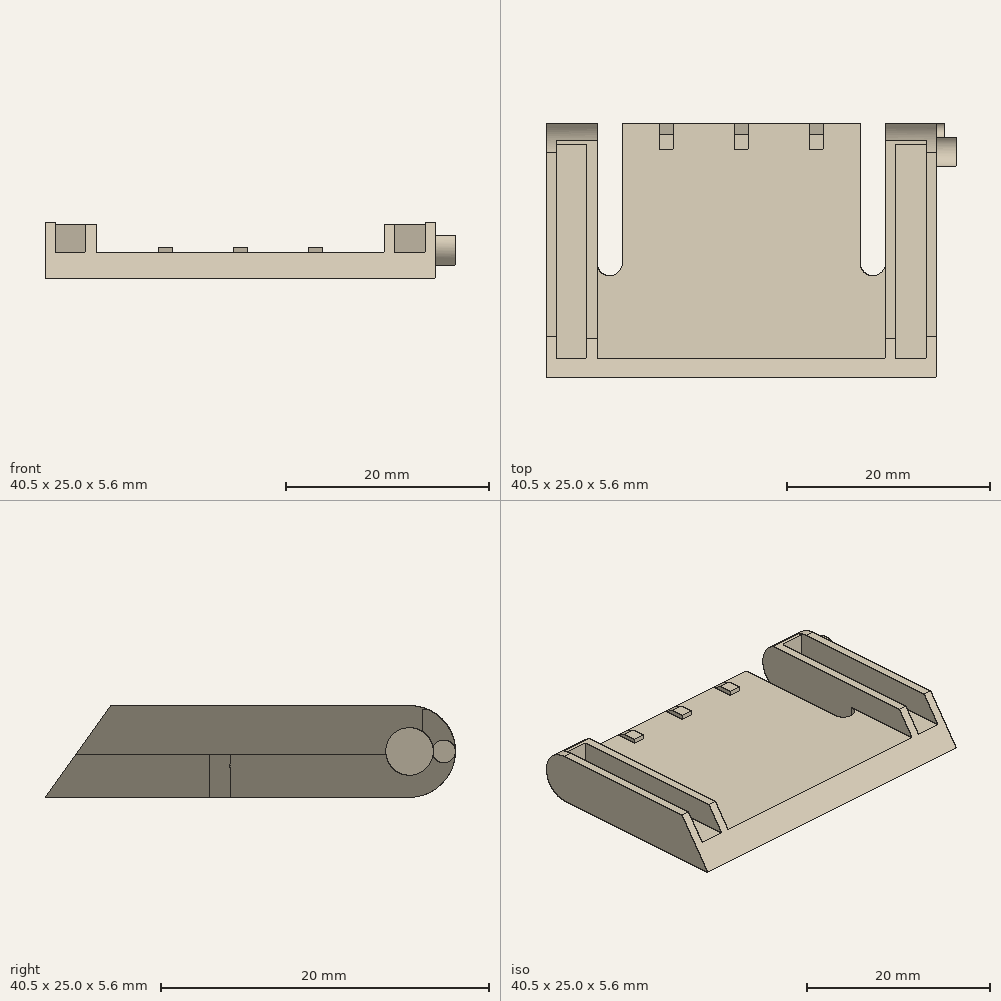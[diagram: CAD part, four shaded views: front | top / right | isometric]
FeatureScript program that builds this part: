
annotation { "Feature Type Name" : "Feature", "Feature Type Description" : "" }
export const myFeature = defineFeature(function(context is Context, id is Id, definition is map)
    precondition{}
    {
        {
            var Q0;
            Q0=qCreatedBy(makeId("Top.planeOp"),FACE);
            var sketch = newSketch(context, id + "F0", { "sketchPlane" : qUnion([Q0])});
            skLineSegment(sketch, "E0.bottom", {"start": v(19.25, -12.5) * mm, "end": v(-19.25, -12.5) * mm});
            skLineSegment(sketch, "E0.top", {"start": v(19.25, 12.5) * mm, "end": v(-19.25, 12.5) * mm});
            skLineSegment(sketch, "E0.left", {"start": v(19.25, -12.5) * mm, "end": v(19.25, 12.5) * mm});
            skLineSegment(sketch, "E0.right", {"start": v(-19.25, -12.5) * mm, "end": v(-19.25, 12.5) * mm});
            skPoint(sketch, "E0.middle", {"position": v(0, 0) * mm});
            skSolve(sketch);
        }
        {
            var Q0;
            Q0 = qSketchRegion(id + "F0", true);
            extrude(context, id + "F1", {"entities" : qUnion([Q0]), "depth" : 2.6 * mm});
        }
        {
            var Q0;
            Q0=makeQuery(id+"F1.opExtrude","CAP_FACE",FACE,{"disambiguationData":[OSD([sQuery(id+"F0.wireOp",EDGE,"E0.bottom"),sQuery(id+"F0.wireOp",EDGE,"E0.top"),sQuery(id+"F0.wireOp",EDGE,"E0.left"),sQuery(id+"F0.wireOp",EDGE,"E0.right")])],"isStart":false});
            var sketch = newSketch(context, id + "F2", { "sketchPlane" : qUnion([Q0])});
            skLineSegment(sketch, "E1.bottom", {"start": v(-14.25, 12.5) * mm, "end": v(-11.75, 12.5) * mm});
            skLineSegment(sketch, "E1.top", {"start": v(-13, -2.5) * mm, "end": v(-13, -2.5) * mm});
            skLineSegment(sketch, "E1.left", {"start": v(-14.25, 12.5) * mm, "end": v(-14.25, -1.25) * mm});
            skLineSegment(sketch, "E1.right", {"start": v(-11.75, 12.5) * mm, "end": v(-11.75, -1.25) * mm});
            skLineSegment(sketch, "E2", {"start": v(0, 12.5) * mm, "end": v(0, -12.5) * mm});
            skLineSegment(sketch, "E3.MirrorCS", {"start": v(14.25, 12.5) * mm, "end": v(11.75, 12.5) * mm});
            skLineSegment(sketch, "E4.MirrorCS", {"start": v(14.25, 12.5) * mm, "end": v(14.25, -1.25) * mm});
            skLineSegment(sketch, "E5.MirrorCS", {"start": v(11.75, 12.5) * mm, "end": v(11.75, -1.25) * mm});
            skLineSegment(sketch, "E6.MirrorCS", {"start": v(13, -2.5) * mm, "end": v(13, -2.5) * mm});
            skPoint(sketch, "E7.visualSharp", {"position": v(-14.25, -2.5) * mm});
            skArc(sketch, "E7.filletArc", {"start": v(-14.25, -1.25) * mm, "mid": v(-13.88, -2.13) * mm, "end": v(-13, -2.5) * mm});
            skPoint(sketch, "E8.visualSharp", {"position": v(-11.75, -2.5) * mm});
            skArc(sketch, "E8.filletArc", {"start": v(-13, -2.5) * mm, "mid": v(-12.12, -2.13) * mm, "end": v(-11.75, -1.25) * mm});
            skPoint(sketch, "E9.visualSharp", {"position": v(11.75, -2.5) * mm});
            skArc(sketch, "E9.filletArc", {"start": v(11.75, -1.25) * mm, "mid": v(12.12, -2.13) * mm, "end": v(13, -2.5) * mm});
            skPoint(sketch, "E10.visualSharp", {"position": v(14.25, -2.5) * mm});
            skArc(sketch, "E10.filletArc", {"start": v(13, -2.5) * mm, "mid": v(13.88, -2.13) * mm, "end": v(14.25, -1.25) * mm});
            skSolve(sketch);
        }
        {
            var Q0;
            Q0 = qSketchRegion(id + "F2", true);
            extrude(context, id + "F3", {"entities" : qUnion([Q0]), "operationType" : NewBodyOperationType.REMOVE, "endBound" : BoundingType.THROUGH_ALL, "oppositeDirection" : true, "depth" : 25 * mm});
        }
        {
            var Q0;
            Q0=makeQuery(id+"F1.opExtrude","CAP_FACE",FACE,{"disambiguationData":[OSD([sQuery(id+"F0.wireOp",EDGE,"E0.bottom"),sQuery(id+"F0.wireOp",EDGE,"E0.top"),sQuery(id+"F0.wireOp",EDGE,"E0.left"),sQuery(id+"F0.wireOp",EDGE,"E0.right")])],"isStart":false});
            var sketch = newSketch(context, id + "F4", { "sketchPlane" : qUnion([Q0])});
            skLineSegment(sketch, "E11.bottom", {"start": v(-19.25, 12.5) * mm, "end": v(-14.25, 12.5) * mm});
            skLineSegment(sketch, "E11.top", {"start": v(-19.25, -12.5) * mm, "end": v(-14.25, -12.5) * mm});
            skLineSegment(sketch, "E11.left", {"start": v(-19.25, 12.5) * mm, "end": v(-19.25, -12.5) * mm});
            skLineSegment(sketch, "E11.right", {"start": v(-14.25, 12.5) * mm, "end": v(-14.25, -12.5) * mm});
            skPoint(sketch, "E12.oppositeSnap0", {"position": v(14.25, 5.62) * mm});
            skLineSegment(sketch, "E12.bottom", {"start": v(19.25, 12.5) * mm, "end": v(14.25, 12.5) * mm});
            skLineSegment(sketch, "E12.top", {"start": v(19.25, -12.5) * mm, "end": v(14.25, -12.5) * mm});
            skLineSegment(sketch, "E12.left", {"start": v(19.25, 12.5) * mm, "end": v(19.25, -12.5) * mm});
            skLineSegment(sketch, "E12.right", {"start": v(14.25, 12.5) * mm, "end": v(14.25, -12.5) * mm});
            skSolve(sketch);
        }
        {
            var Q0;
            Q0 = qSketchRegion(id + "F4", true);
            extrude(context, id + "F5", {"entities" : qUnion([Q0]), "operationType" : NewBodyOperationType.ADD, "depth" : 3 * mm});
        }
        {
            var Q0;
            Q0=makeQuery(id+"F5.boolean.opBoolean","MERGE",FACE,{"derivedFrom":[makeQuery(id+"F1.opExtrude","SWEPT_FACE",FACE,{"disambiguationData":[OSD([sQuery(id+"F0.wireOp",EDGE,"E0.bottom")])]}),makeQuery(id+"F5.opExtrude","SWEPT_FACE",FACE,{"disambiguationData":[OSD([sQuery(id+"F4.wireOp",EDGE,"E11.top")])]}),makeQuery(id+"F5.opExtrude","SWEPT_FACE",FACE,{"disambiguationData":[OSD([sQuery(id+"F4.wireOp",EDGE,"E12.top")])]})]});
            var sketch = newSketch(context, id + "F6", { "sketchPlane" : qUnion([Q0])});
            skLineSegment(sketch, "E13.bottom", {"start": v(-18.25, 5.6) * mm, "end": v(-15.25, 5.6) * mm});
            skLineSegment(sketch, "E13.top", {"start": v(-18.25, 2.6) * mm, "end": v(-15.25, 2.6) * mm});
            skLineSegment(sketch, "E13.left", {"start": v(-18.25, 5.6) * mm, "end": v(-18.25, 2.6) * mm});
            skLineSegment(sketch, "E13.right", {"start": v(-15.25, 5.6) * mm, "end": v(-15.25, 2.6) * mm});
            skLineSegment(sketch, "E14.bottom", {"start": v(15.25, 5.6) * mm, "end": v(18.25, 5.6) * mm});
            skLineSegment(sketch, "E14.top", {"start": v(15.25, 2.6) * mm, "end": v(18.25, 2.6) * mm});
            skLineSegment(sketch, "E14.left", {"start": v(15.25, 5.6) * mm, "end": v(15.25, 2.6) * mm});
            skLineSegment(sketch, "E14.right", {"start": v(18.25, 5.6) * mm, "end": v(18.25, 2.6) * mm});
            skSolve(sketch);
        }
        {
            var Q0;
            Q0 = qSketchRegion(id + "F6", true);
            extrude(context, id + "F7", {"entities" : qUnion([Q0]), "operationType" : NewBodyOperationType.REMOVE, "oppositeDirection" : true, "depth" : 23 * mm});
        }
        {
            var Q0;
            Q0=makeQuery(id+"F5.opExtrude","CAP_EDGE",EDGE,{"disambiguationData":[OSD([sQuery(id+"F4.wireOp",EDGE,"E12.bottom")])],"isStart":false});
            var Q1;
            {var subQ0=sQuery(id+"F0.wireOp",EDGE,"E0.left");var subQ1=sQuery(id+"F0.wireOp",EDGE,"E0.top");Q1=makeQuery(id+"F3.boolean.opBoolean","SPLIT",EDGE,{"disambiguationData":[TD([makeQuery(id+"F1.opExtrude","SWEPT_FACE",FACE,{"disambiguationData":[OSD([subQ0])]})])],"derivedFrom":makeQuery(id+"F1.opExtrude","CAP_EDGE",EDGE,{"disambiguationData":[OSD([subQ1])],"isStart":true})});}
            var Q2;
            Q2=makeQuery(id+"F5.opExtrude","CAP_EDGE",EDGE,{"disambiguationData":[OSD([sQuery(id+"F4.wireOp",EDGE,"E11.bottom")])],"isStart":false});
            var Q3;
            {var subQ0=sQuery(id+"F0.wireOp",EDGE,"E0.right");var subQ1=sQuery(id+"F0.wireOp",EDGE,"E0.top");Q3=makeQuery(id+"F3.boolean.opBoolean","SPLIT",EDGE,{"disambiguationData":[TD([makeQuery(id+"F1.opExtrude","SWEPT_FACE",FACE,{"disambiguationData":[OSD([subQ0])]})])],"derivedFrom":makeQuery(id+"F1.opExtrude","CAP_EDGE",EDGE,{"disambiguationData":[OSD([subQ1])],"isStart":true})});}
            var Q4;
            {var subQ0=sQuery(id+"F0.wireOp",EDGE,"E0.top");Q4=makeQuery(id+"F3.boolean.opBoolean","SPLIT",EDGE,{"disambiguationData":[TD([makeQuery(id+"F3.opExtrude","SWEPT_FACE",FACE,{"disambiguationData":[OSD([sQuery(id+"F2.wireOp",EDGE,"E1.right")])]})])],"derivedFrom":makeQuery(id+"F1.opExtrude","CAP_EDGE",EDGE,{"disambiguationData":[OSD([subQ0])],"isStart":true})});}
            fillet(context, id + "F8", {"entities" : qUnion([Q0, Q1, Q2, Q3, Q4]), "radius" : 2.8 * mm, "tangentPropagation" : true, "allowEdgeOverflow" : false});
        }
        {
            var Q0;
            Q0=makeQuery(id+"F5.boolean.opBoolean","MERGE",FACE,{"derivedFrom":[makeQuery(id+"F1.opExtrude","SWEPT_FACE",FACE,{"disambiguationData":[OSD([sQuery(id+"F0.wireOp",EDGE,"E0.bottom")])]}),makeQuery(id+"F5.opExtrude","SWEPT_FACE",FACE,{"disambiguationData":[OSD([sQuery(id+"F4.wireOp",EDGE,"E11.top")])]}),makeQuery(id+"F5.opExtrude","SWEPT_FACE",FACE,{"disambiguationData":[OSD([sQuery(id+"F4.wireOp",EDGE,"E12.top")])]})]});
            var sketch = newSketch(context, id + "F9", { "sketchPlane" : qUnion([Q0])});
            skLineSegment(sketch, "E15.bottom", {"start": v(-14.25, 5.6) * mm, "end": v(-15.25, 5.6) * mm});
            skLineSegment(sketch, "E15.top", {"start": v(-14.25, 5.35) * mm, "end": v(-15.25, 5.35) * mm});
            skLineSegment(sketch, "E15.left", {"start": v(-14.25, 5.6) * mm, "end": v(-14.25, 5.35) * mm});
            skLineSegment(sketch, "E15.right", {"start": v(-15.25, 5.6) * mm, "end": v(-15.25, 5.35) * mm});
            skLineSegment(sketch, "E16.bottom", {"start": v(14.25, 5.6) * mm, "end": v(15.25, 5.6) * mm});
            skLineSegment(sketch, "E16.top", {"start": v(14.25, 5.35) * mm, "end": v(15.25, 5.35) * mm});
            skLineSegment(sketch, "E16.left", {"start": v(14.25, 5.6) * mm, "end": v(14.25, 5.35) * mm});
            skLineSegment(sketch, "E16.right", {"start": v(15.25, 5.6) * mm, "end": v(15.25, 5.35) * mm});
            skLineSegment(sketch, "E17.bottom", {"start": v(-15.25, 5.6) * mm, "end": v(-18.25, 5.6) * mm});
            skLineSegment(sketch, "E17.top", {"start": v(-15.25, 5.35) * mm, "end": v(-18.25, 5.35) * mm});
            skLineSegment(sketch, "E17.right", {"start": v(-18.25, 5.6) * mm, "end": v(-18.25, 5.35) * mm});
            skLineSegment(sketch, "E18.bottom", {"start": v(15.25, 5.6) * mm, "end": v(18.25, 5.6) * mm});
            skLineSegment(sketch, "E18.top", {"start": v(15.25, 5.35) * mm, "end": v(18.25, 5.35) * mm});
            skLineSegment(sketch, "E18.right", {"start": v(18.25, 5.6) * mm, "end": v(18.25, 5.35) * mm});
            skSolve(sketch);
        }
        {
            var Q0;
            Q0 = qSketchRegion(id + "F9", true);
            extrude(context, id + "F10", {"entities" : qUnion([Q0]), "operationType" : NewBodyOperationType.REMOVE, "endBound" : BoundingType.THROUGH_ALL, "oppositeDirection" : true, "depth" : 25 * mm});
        }
        {
            var Q0;
            Q0=makeQuery(id+"F5.boolean.opBoolean","MERGE",FACE,{"derivedFrom":[makeQuery(id+"F1.opExtrude","SWEPT_FACE",FACE,{"disambiguationData":[OSD([sQuery(id+"F0.wireOp",EDGE,"E0.left")])]}),makeQuery(id+"F5.opExtrude","SWEPT_FACE",FACE,{"disambiguationData":[OSD([sQuery(id+"F4.wireOp",EDGE,"E12.left")])]})]});
            var sketch = newSketch(context, id + "F11", { "sketchPlane" : qUnion([Q0])});
            skCircle(sketch, "E19", {"center": v(9.7, 2.8) * mm, "radius": 1.45 * mm});
            skCircle(sketch, "E20", {"center": v(11.8, 2.8) * mm, "radius": 0.7 * mm});
            skSolve(sketch);
        }
        {
            var Q0;
            {var subQ0=sQuery(id+"F11.wireOp",EDGE,"E20");var subQ1=sQuery(id+"F11.wireOp",EDGE,"E19");var subQ2=makeQuery(id+"F11.imprint","INTERSECT",VERTEX,{"disambiguationData":[OD(0.0)],"derivedFrom":[subQ1,subQ0]});Q0=makeQuery(id+"F11.imprint","IMPRINT",FACE,{"disambiguationData":[TD([[makeQuery(id+"F11.imprint","IMPRINT",EDGE,{"disambiguationData":[TD([[subQ2,-1.0]])],"derivedFrom":subQ1}),1.0]])]});}
            var Q1;
            {var subQ0=sQuery(id+"F11.wireOp",EDGE,"E20");var subQ1=sQuery(id+"F11.wireOp",EDGE,"E19");var subQ2=makeQuery(id+"F11.imprint","INTERSECT",VERTEX,{"disambiguationData":[OD(0.0)],"derivedFrom":[subQ1,subQ0]});Q1=makeQuery(id+"F11.imprint","IMPRINT",FACE,{"disambiguationData":[TD([[makeQuery(id+"F11.imprint","IMPRINT",EDGE,{"disambiguationData":[TD([[subQ2,1.0]])],"derivedFrom":subQ1}),1.0]])]});}
            extrude(context, id + "F12", {"entities" : qUnion([Q0, Q1]), "operationType" : NewBodyOperationType.ADD, "depth" : 2 * mm});
        }
        {
            var Q0;
            {var subQ0=sQuery(id+"F11.wireOp",EDGE,"E20");var subQ1=sQuery(id+"F11.wireOp",EDGE,"E19");var subQ2=makeQuery(id+"F11.imprint","INTERSECT",VERTEX,{"disambiguationData":[OD(0.0)],"derivedFrom":[subQ1,subQ0]});Q0=makeQuery(id+"F11.imprint","IMPRINT",FACE,{"disambiguationData":[TD([[makeQuery(id+"F11.imprint","IMPRINT",EDGE,{"disambiguationData":[TD([[subQ2,1.0]])],"derivedFrom":subQ1}),-1.0]])]});}
            extrude(context, id + "F13", {"entities" : qUnion([Q0]), "operationType" : NewBodyOperationType.ADD, "depth" : 0.8 * mm});
        }
        {
            var Q0;
            Q0=makeQuery(id+"F5.boolean.opBoolean","MERGE",FACE,{"derivedFrom":[makeQuery(id+"F1.opExtrude","SWEPT_FACE",FACE,{"disambiguationData":[OSD([sQuery(id+"F0.wireOp",EDGE,"E0.left")])]}),makeQuery(id+"F5.opExtrude","SWEPT_FACE",FACE,{"disambiguationData":[OSD([sQuery(id+"F4.wireOp",EDGE,"E12.left")])]})]});
            var sketch = newSketch(context, id + "F14", { "sketchPlane" : qUnion([Q0])});
            skLineSegment(sketch, "E21", {"start": v(-12.5, 0) * mm, "end": v(-8.5, 5.6) * mm});
            skSolve(sketch);
        }
        {
            var Q0;
            Q0=makeQuery(id+"F1.opExtrude","CAP_FACE",FACE,{"disambiguationData":[OSD([sQuery(id+"F0.wireOp",EDGE,"E0.bottom"),sQuery(id+"F0.wireOp",EDGE,"E0.top"),sQuery(id+"F0.wireOp",EDGE,"E0.left"),sQuery(id+"F0.wireOp",EDGE,"E0.right")])],"isStart":false});
            var sketch = newSketch(context, id + "F15", { "sketchPlane" : qUnion([Q0])});
            skLineSegment(sketch, "E22.top", {"start": v(-0.7, 10) * mm, "end": v(0.7, 10) * mm});
            skLineSegment(sketch, "E22.left", {"start": v(-0.7, 12.5) * mm, "end": v(-0.7, 10) * mm});
            skLineSegment(sketch, "E22.right", {"start": v(0.7, 12.5) * mm, "end": v(0.7, 10) * mm});
            skLineSegment(sketch, "E23", {"start": v(-0.7, 12.5) * mm, "end": v(0.7, 12.5) * mm});
            skLineSegment(sketch, "E24.1.0.0", {"start": v(6.7, 12.5) * mm, "end": v(8.1, 12.5) * mm});
            skLineSegment(sketch, "E24.1.0.1", {"start": v(6.7, 12.5) * mm, "end": v(6.7, 10) * mm});
            skLineSegment(sketch, "E24.1.0.2", {"start": v(6.7, 10) * mm, "end": v(8.1, 10) * mm});
            skLineSegment(sketch, "E24.1.0.3", {"start": v(8.1, 12.5) * mm, "end": v(8.1, 10) * mm});
            skLineSegment(sketch, "E24.direction1", {"start": v(-0.7, 12.5) * mm, "end": v(6.7, 12.5) * mm, "construction": true});
            skLineSegment(sketch, "E25", {"start": v(0, 12.5) * mm, "end": v(0, 10) * mm});
            skLineSegment(sketch, "E26.MirrorCS", {"start": v(-6.7, 12.5) * mm, "end": v(-8.1, 12.5) * mm});
            skLineSegment(sketch, "E27.MirrorCS", {"start": v(-6.7, 12.5) * mm, "end": v(-6.7, 10) * mm});
            skLineSegment(sketch, "E28.MirrorCS", {"start": v(-8.1, 12.5) * mm, "end": v(-8.1, 10) * mm});
            skLineSegment(sketch, "E29.MirrorCS", {"start": v(-6.7, 10) * mm, "end": v(-8.1, 10) * mm});
            skSolve(sketch);
        }
        {
            var Q0;
            Q0=makeQuery(id+"F15.imprint","IMPRINT",FACE,{"disambiguationData":[TD([[makeQuery(id+"F15.imprint","IMPRINT",EDGE,{"derivedFrom":sQuery(id+"F15.wireOp",EDGE,"E26.MirrorCS")}),1.0]])]});
            var Q1;
            {var subQ0=sQuery(id+"F15.wireOp",EDGE,"E22.left");Q1=makeQuery(id+"F15.imprint","IMPRINT",FACE,{"disambiguationData":[TD([[makeQuery(id+"F15.imprint","IMPRINT",EDGE,{"derivedFrom":subQ0}),1.0]])]});}
            var Q2;
            {var subQ0=sQuery(id+"F15.wireOp",EDGE,"E22.right");Q2=makeQuery(id+"F15.imprint","IMPRINT",FACE,{"disambiguationData":[TD([[makeQuery(id+"F15.imprint","IMPRINT",EDGE,{"derivedFrom":subQ0}),-1.0]])]});}
            var Q3;
            Q3=makeQuery(id+"F15.imprint","IMPRINT",FACE,{"disambiguationData":[TD([[makeQuery(id+"F15.imprint","IMPRINT",EDGE,{"derivedFrom":sQuery(id+"F15.wireOp",EDGE,"E24.1.0.0")}),1.0]])]});
            extrude(context, id + "F16", {"entities" : qUnion([Q0, Q1, Q2, Q3]), "operationType" : NewBodyOperationType.ADD, "depth" : 0.5 * mm});
        }
        {
            var Q0;
            Q0=makeQuery(id+"F16.opExtrude","CAP_EDGE",EDGE,{"disambiguationData":[OSD([sQuery(id+"F15.wireOp",EDGE,"E26.MirrorCS")])],"isStart":false});
            var Q1;
            Q1=makeQuery(id+"F16.opExtrude","CAP_EDGE",EDGE,{"disambiguationData":[OSD([sQuery(id+"F15.wireOp",EDGE,"E23")])],"isStart":false});
            var Q2;
            Q2=makeQuery(id+"F16.opExtrude","CAP_EDGE",EDGE,{"disambiguationData":[OSD([sQuery(id+"F15.wireOp",EDGE,"E24.1.0.0")])],"isStart":false});
            chamfer(context, id + "F17", {"entities" : qUnion([Q0, Q1, Q2]), "chamferType" : ChamferType.TWO_OFFSETS, "width1" : 1 * mm, "oppositeDirection" : false, "width2" : 0.5 * mm, "tangentPropagation" : true});
        }
        {
            var Q0;
            {var subQ0=sQuery(id+"F14.wireOp",EDGE,"E21");Q0=makeQuery(id+"F14.imprint","IMPRINT",FACE,{"disambiguationData":[TD([[makeQuery(id+"F14.imprint","IMPRINT",EDGE,{"derivedFrom":subQ0}),1.0]])]});}
            extrude(context, id + "F18", {"entities" : qUnion([Q0]), "operationType" : NewBodyOperationType.REMOVE, "endBound" : BoundingType.THROUGH_ALL, "oppositeDirection" : true, "depth" : 25 * mm});
        }
    });
